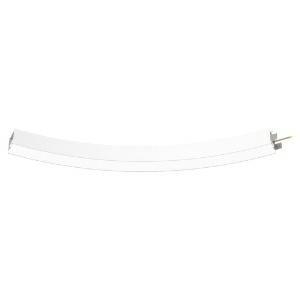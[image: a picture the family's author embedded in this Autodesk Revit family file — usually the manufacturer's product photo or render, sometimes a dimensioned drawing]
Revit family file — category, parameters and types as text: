
# Revit family: super-g_slim_super_g_slim_dir_ind_3000_45deg_hl_ps_led_36w__5760lm__3000k__cri80_430-3800_2671
name_source: partatom
category: Leuchten
revit_build: Autodesk Revit 2016 (Build: 20190508_0715(x64)
units: mm (PartAtom-declared; Revit-internal decimal feet)

## family parameters
Basisbauteil = Fläche
Beim Laden mit Abzugskörper schneiden = Nein
Bemaßung runder Anschluss = Durchmesser verwenden
Gemeinsam genutzt = Nein
Lichtquelle = Nein
Raumberechnungspunkt = Nein
Teiletyp = Normal

## types (1)
- 430-3800-D01 (1 x LED, 720 lm, 3000K)
    Beschreibung = The insert consists of aluminum-extruded profile. Charming SOFT-EDGE design ensure unparalleled styling. The ballast is integrated and allows for an operation with 220-240V (50/60Hz). SUPER-G SLIM (# 430-3800) ist not dimmable (on/off).
    CIE Flux Codes = 48 79 96 66 85
    Color Rendering = 1B/80…89
    Color Temperature = 3000K
    Height = 90 mm
    Hersteller = Prolicht
    Lamp Light Flux = 720 lm
    Lamp count = 1
    Lampe = 1 x LED
    Length = 144 mm
    Luminous efficacy = 122 lm/W
    ModVariant = Nein
    Modell = 430-3800
    Mounting Place = Ceiling
    Mounting Type = Pendant
    Number of Poles = 1
    OnlyDefault = Ja
    Power Factor = 1
    Product Name = SUPER-G SLIM__SUPER G SLIM DIR/IND 3000/45° HL PS LED 36W  5760lm  3000K  CRI80
    Product group = Suspended profile systems
    ProductGroupID = 944
    Protection Class = Protection class
    Protection Degree = Degree of protection
    RLX_Detail_Level = 1
    RlxData = <blob elided: 29065 chars, md5=7db82851>
    Scheinlast = 40 VA
    Socket = socket
    Standby Power = 0 W
    System Light Flux = 4873 lm
    System Power = 40 W
    Typenbild = 430-3800.jpg
    URL = http://relux.com
    VarID = 430-3800-d01
    Voltage = 0 V
    Vorgabe-Ansicht = 1800 mm
    Weight = 0.00 kg
    Width = 65 mm

## geometry (parser evidence)
native form markers: Blend x4, Sweep x41
no freeform markers — native parametric forms only
